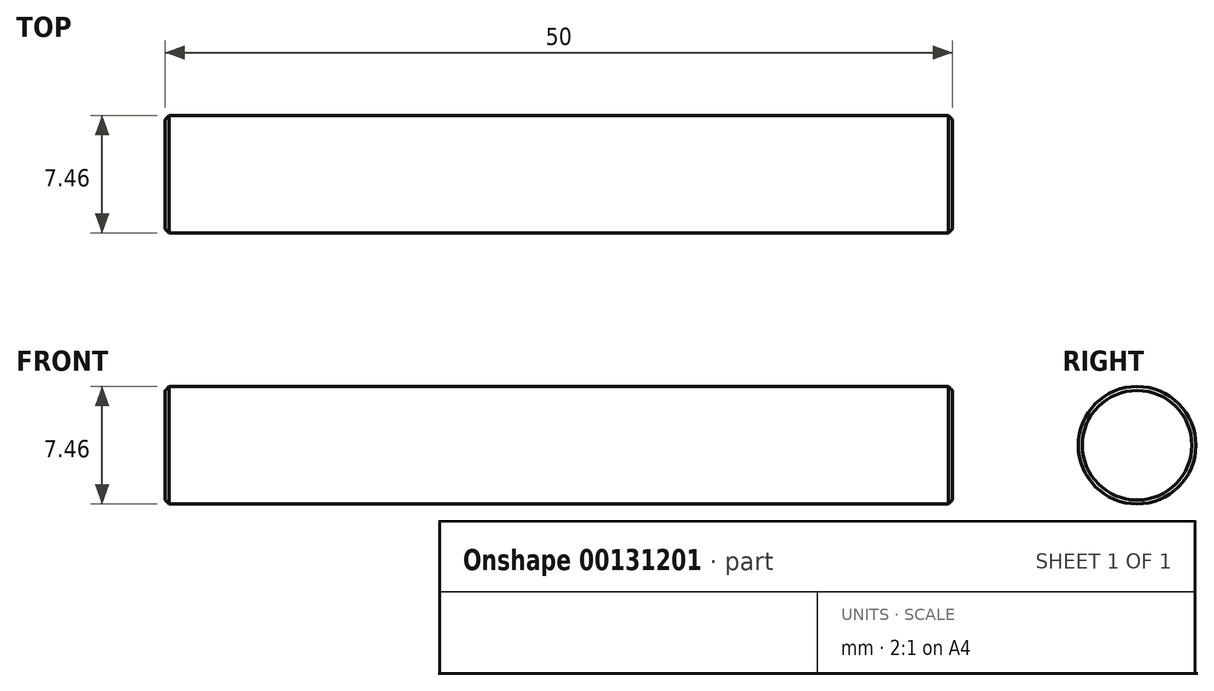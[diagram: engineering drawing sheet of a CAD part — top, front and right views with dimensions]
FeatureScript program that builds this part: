
annotation { "Feature Type Name" : "Feature", "Feature Type Description" : "" }
export const myFeature = defineFeature(function(context is Context, id is Id, definition is map)
    precondition{}
    {
        {
            var Q0;
            Q0=qCreatedBy(makeId("Front.planeOp"),FACE);
            var sketch = newSketch(context, id + "F0", { "sketchPlane" : qUnion([Q0])});
            skLineSegment(sketch, "E0.bottom", {"start": v(25, 3.73) * mm, "end": v(-25, 3.73) * mm});
            skLineSegment(sketch, "E0.left", {"start": v(25, 3.73) * mm, "end": v(25, 0) * mm});
            skLineSegment(sketch, "E0.right", {"start": v(-25, 3.73) * mm, "end": v(-25, 0) * mm});
            skPoint(sketch, "E0.middle", {"position": v(0, 0) * mm});
            skLineSegment(sketch, "E1", {"start": v(0, 0) * mm, "end": v(45.28, 0) * mm});
            skLineSegment(sketch, "E2", {"start": v(0, 0) * mm, "end": v(-33.57, 0) * mm});
            skPoint(sketch, "E3.orphan", {"position": v(-25, -3.73) * mm});
            skPoint(sketch, "E4.orphan", {"position": v(25, -3.73) * mm});
            skSolve(sketch);
        }
        {
            var Q0;
            Q0=makeQuery(id+"F0.imprint","IMPRINT",FACE,{"disambiguationData":[TD([[makeQuery(id+"F0.imprint","IMPRINT",EDGE,{"derivedFrom":sQuery(id+"F0.wireOp",EDGE,"E0.bottom")}),1.0]])]});
            var Q1;
            Q1=sQuery(id+"F0.wireOp",EDGE,"E2");
            revolve(context, id + "F1", {"entities" : qUnion([Q0]), "axis" : qUnion([Q1]), "revolveType" : RevolveType.FULL});
        }
        {
            var Q0;
            Q0=makeQuery(id+"F1.opRevolve","SWEPT_EDGE",EDGE,{"disambiguationData":[OSD([sQuery(id+"F0.wireOp",EDGE,"E0.bottom"),sQuery(id+"F0.wireOp",EDGE,"E0.left")])]});
            var Q1;
            Q1=makeQuery(id+"F1.opRevolve","SWEPT_EDGE",EDGE,{"disambiguationData":[OSD([sQuery(id+"F0.wireOp",EDGE,"E0.bottom"),sQuery(id+"F0.wireOp",EDGE,"E0.right")])]});
            chamfer(context, id + "F2", {"entities" : qUnion([Q0, Q1]), "width" : 0.25 * mm, "tangentPropagation" : true});
        }
    });
